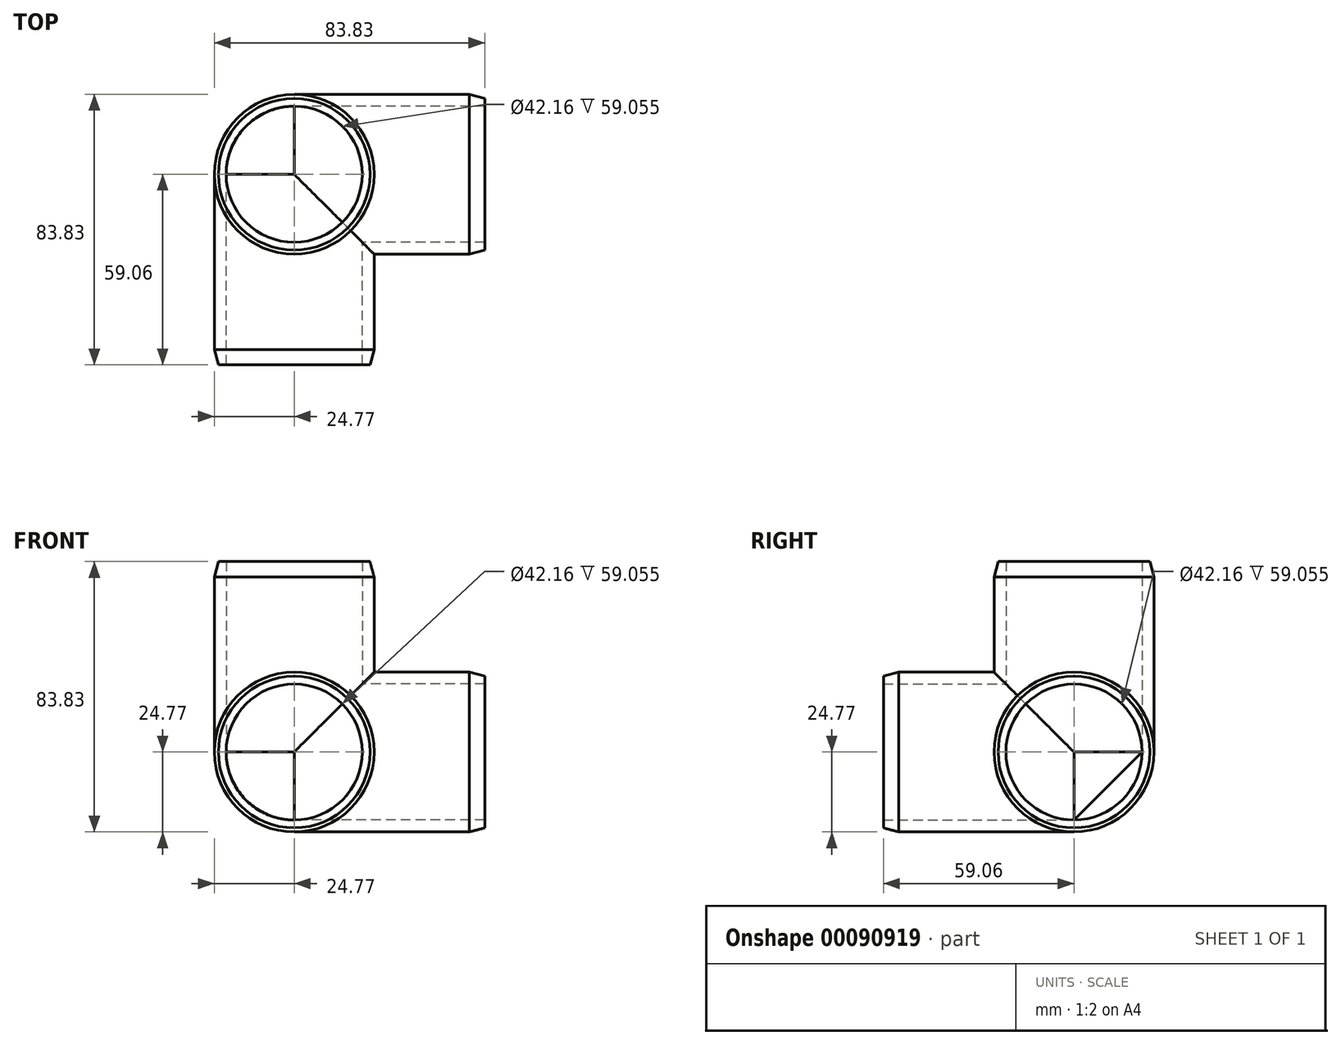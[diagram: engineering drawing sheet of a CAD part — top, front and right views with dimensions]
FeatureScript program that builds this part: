
annotation { "Feature Type Name" : "Feature", "Feature Type Description" : "" }
export const myFeature = defineFeature(function(context is Context, id is Id, definition is map)
    precondition{}
    {
        {
            var Q0;
            Q0=qCreatedBy(makeId("Front.planeOp"),FACE);
            var sketch = newSketch(context, id + "F0", { "sketchPlane" : qUnion([Q0])});
            skCircle(sketch, "E0", {"center": v(0, 0) * mm, "radius": 21.08 * mm});
            skCircle(sketch, "E1.0", {"center": v(0, 0) * mm, "radius": 24.77 * mm});
            skSolve(sketch);
        }
        {
            var Q0;
            Q0 = qSketchRegion(id + "F0", true);
            extrude(context, id + "F1", {"entities" : qUnion([Q0]), "depth" : 59.05 * mm});
        }
        {
            var Q0;
            Q0=qCreatedBy(makeId("Top.planeOp"),FACE);
            var sketch = newSketch(context, id + "F2", { "sketchPlane" : qUnion([Q0])});
            skCircle(sketch, "E2", {"center": v(0, 0) * mm, "radius": 21.08 * mm});
            skCircle(sketch, "E3.0", {"center": v(0, 0) * mm, "radius": 24.77 * mm});
            skSolve(sketch);
        }
        {
            var Q0;
            Q0 = qSketchRegion(id + "F2", true);
            extrude(context, id + "F3", {"entities" : qUnion([Q0]), "operationType" : NewBodyOperationType.ADD, "depth" : 59.05 * mm});
        }
        {
            var Q0;
            Q0=qCreatedBy(makeId("Right.planeOp"),FACE);
            var sketch = newSketch(context, id + "F4", { "sketchPlane" : qUnion([Q0])});
            skCircle(sketch, "E4", {"center": v(0, 0) * mm, "radius": 21.08 * mm});
            skCircle(sketch, "E5.0", {"center": v(0, 0) * mm, "radius": 24.77 * mm});
            skSolve(sketch);
        }
        {
            var Q0;
            Q0 = qSketchRegion(id + "F4", true);
            extrude(context, id + "F5", {"entities" : qUnion([Q0]), "operationType" : NewBodyOperationType.ADD, "depth" : 59.05 * mm});
        }
        {
            var Q0;
            Q0=makeQuery(id+"F4.imprint","IMPRINT",FACE,{"disambiguationData":[TD([[makeQuery(id+"F4.imprint","IMPRINT",EDGE,{"derivedFrom":sQuery(id+"F4.wireOp",EDGE,"E4")}),1.0]])]});
            extrude(context, id + "F6", {"entities" : qUnion([Q0]), "operationType" : NewBodyOperationType.REMOVE, "endBound" : BoundingType.THROUGH_ALL, "depth" : 25.4 * mm});
        }
        {
            var Q0;
            Q0=makeQuery(id+"F2.imprint","IMPRINT",FACE,{"disambiguationData":[TD([[makeQuery(id+"F2.imprint","IMPRINT",EDGE,{"derivedFrom":sQuery(id+"F2.wireOp",EDGE,"E2")}),1.0]])]});
            extrude(context, id + "F7", {"entities" : qUnion([Q0]), "operationType" : NewBodyOperationType.REMOVE, "endBound" : BoundingType.THROUGH_ALL, "depth" : 25.4 * mm});
        }
        {
            var Q0;
            Q0=makeQuery(id+"F0.imprint","IMPRINT",FACE,{"disambiguationData":[TD([[makeQuery(id+"F0.imprint","IMPRINT",EDGE,{"derivedFrom":sQuery(id+"F0.wireOp",EDGE,"E0")}),1.0]])]});
            extrude(context, id + "F8", {"entities" : qUnion([Q0]), "operationType" : NewBodyOperationType.REMOVE, "endBound" : BoundingType.THROUGH_ALL, "depth" : 25.4 * mm});
        }
        {
            var Q0;
            {var subQ0=sQuery(id+"F0.wireOp",EDGE,"E1.0");var subQ1=makeQuery(id+"F1.opExtrude","SWEPT_FACE",FACE,{"disambiguationData":[OSD([subQ0])]});var subQ2=sQuery(id+"F2.wireOp",EDGE,"E2");var subQ3=makeQuery(id+"F3.opExtrude","SWEPT_FACE",FACE,{"disambiguationData":[OSD([subQ2])]});var subQ4=sQuery(id+"F0.wireOp",EDGE,"E0");var subQ5=makeQuery(id+"F1.opExtrude","CAP_FACE",FACE,{"disambiguationData":[OSD([subQ4,subQ0])],"isStart":true});var subQ6=makeQuery(id+"F1.opExtrude","SWEPT_FACE",FACE,{"disambiguationData":[OSD([subQ4])]});var subQ7=sQuery(id+"F2.wireOp",EDGE,"E3.0");var subQ8=makeQuery(id+"F3.opExtrude","CAP_FACE",FACE,{"disambiguationData":[OSD([subQ2,subQ7])],"isStart":true});var subQ9=makeQuery(id+"F3.opExtrude","SWEPT_FACE",FACE,{"disambiguationData":[OSD([subQ7])]});var subQ10=sQuery(id+"F4.wireOp",EDGE,"E4");var subQ11=sQuery(id+"F4.wireOp",EDGE,"E5.0");Q0=makeQuery(id+"F5.boolean.opBoolean","SPLIT",FACE,{"disambiguationData":[TD([subQ6,subQ5,subQ1,subQ3,subQ8,subQ9,makeQuery(id+"F5.opExtrude","SWEPT_FACE",FACE,{"disambiguationData":[OSD([subQ10])]}),makeQuery(id+"F5.opExtrude","CAP_FACE",FACE,{"disambiguationData":[OSD([subQ10,subQ11])],"isStart":true}),makeQuery(id+"F5.opExtrude","SWEPT_FACE",FACE,{"disambiguationData":[OSD([subQ11])]})])],"derivedFrom":makeQuery(id+"F3.boolean.opBoolean","SPLIT",FACE,{"disambiguationData":[TD([subQ6,subQ5,subQ1,subQ3,subQ8,subQ9])],"derivedFrom":subQ5})});}
            var Q1;
            {var subQ0=sQuery(id+"F0.wireOp",EDGE,"E1.0");var subQ1=makeQuery(id+"F1.opExtrude","SWEPT_FACE",FACE,{"disambiguationData":[OSD([subQ0])]});var subQ2=sQuery(id+"F2.wireOp",EDGE,"E2");var subQ3=makeQuery(id+"F3.opExtrude","SWEPT_FACE",FACE,{"disambiguationData":[OSD([subQ2])]});var subQ4=sQuery(id+"F0.wireOp",EDGE,"E0");var subQ5=makeQuery(id+"F1.opExtrude","CAP_FACE",FACE,{"disambiguationData":[OSD([subQ4,subQ0])],"isStart":true});var subQ6=makeQuery(id+"F1.opExtrude","SWEPT_FACE",FACE,{"disambiguationData":[OSD([subQ4])]});var subQ7=sQuery(id+"F2.wireOp",EDGE,"E3.0");var subQ8=makeQuery(id+"F3.opExtrude","CAP_FACE",FACE,{"disambiguationData":[OSD([subQ2,subQ7])],"isStart":true});var subQ9=makeQuery(id+"F3.opExtrude","SWEPT_FACE",FACE,{"disambiguationData":[OSD([subQ7])]});var subQ10=sQuery(id+"F4.wireOp",EDGE,"E4");var subQ11=sQuery(id+"F4.wireOp",EDGE,"E5.0");Q1=makeQuery(id+"F5.boolean.opBoolean","SPLIT",FACE,{"disambiguationData":[TD([subQ6,subQ5,subQ1,subQ3,subQ8,subQ9,makeQuery(id+"F5.opExtrude","SWEPT_FACE",FACE,{"disambiguationData":[OSD([subQ10])]}),makeQuery(id+"F5.opExtrude","CAP_FACE",FACE,{"disambiguationData":[OSD([subQ10,subQ11])],"isStart":true}),makeQuery(id+"F5.opExtrude","SWEPT_FACE",FACE,{"disambiguationData":[OSD([subQ11])]})])],"derivedFrom":makeQuery(id+"F3.boolean.opBoolean","SPLIT",FACE,{"disambiguationData":[TD([subQ6,subQ5,subQ1,subQ3,subQ8,subQ9])],"derivedFrom":subQ8})});}
            var Q2;
            Q2=makeQuery(id+"F5.boolean.opBoolean","SPLIT",EDGE,{"disambiguationData":[OD(1.0)],"derivedFrom":makeQuery(id+"F5.opExtrude","CAP_EDGE",EDGE,{"disambiguationData":[OSD([sQuery(id+"F4.wireOp",EDGE,"E4")])],"isStart":true})});
            var Q3;
            {var subQ0=sQuery(id+"F0.wireOp",EDGE,"E1.0");var subQ1=sQuery(id+"F2.wireOp",EDGE,"E3.0");var subQ2=sQuery(id+"F4.wireOp",EDGE,"E5.0");Q3=makeQuery(id+"F5.boolean.opBoolean","SPLIT",EDGE,{"disambiguationData":[TD([makeQuery(id+"F1.opExtrude","CAP_FACE",FACE,{"disambiguationData":[OSD([sQuery(id+"F0.wireOp",EDGE,"E0"),subQ0])],"isStart":true}),makeQuery(id+"F1.opExtrude","SWEPT_FACE",FACE,{"disambiguationData":[OSD([subQ0])]}),makeQuery(id+"F3.opExtrude","CAP_FACE",FACE,{"disambiguationData":[OSD([sQuery(id+"F2.wireOp",EDGE,"E2"),subQ1])],"isStart":true}),makeQuery(id+"F3.opExtrude","SWEPT_FACE",FACE,{"disambiguationData":[OSD([subQ1])]}),makeQuery(id+"F5.opExtrude","CAP_FACE",FACE,{"disambiguationData":[OSD([sQuery(id+"F4.wireOp",EDGE,"E4"),subQ2])],"isStart":true}),makeQuery(id+"F5.opExtrude","SWEPT_FACE",FACE,{"disambiguationData":[OSD([subQ2])]})])],"derivedFrom":makeQuery(id+"F5.opExtrude","CAP_EDGE",EDGE,{"disambiguationData":[OSD([subQ2])],"isStart":true})});}
            loft(context, id + "F9", {"operationType" : NewBodyOperationType.ADD, "addGuides" : true, "sheetProfilesArray" : [{ "sheetProfileEntities" : qUnion([Q0]) }, { "sheetProfileEntities" : qUnion([Q1]) }], "guidesArray" : [{ "guideEntities" : qUnion([Q2]), "guideDerivativeType" : LoftGuideDerivativeType.DEFAULT, "guideDerivativeMagnitude" : 1 }, { "guideEntities" : qUnion([Q3]), "guideDerivativeType" : LoftGuideDerivativeType.DEFAULT, "guideDerivativeMagnitude" : 1 }]});
        }
        {
            var Q0;
            Q0=makeQuery(id+"F3.opExtrude","CAP_EDGE",EDGE,{"disambiguationData":[OSD([sQuery(id+"F2.wireOp",EDGE,"E3.0")])],"isStart":false});
            var Q1;
            Q1=makeQuery(id+"F1.opExtrude","CAP_EDGE",EDGE,{"disambiguationData":[OSD([sQuery(id+"F0.wireOp",EDGE,"E1.0")])],"isStart":false});
            var Q2;
            Q2=makeQuery(id+"F5.opExtrude","CAP_EDGE",EDGE,{"disambiguationData":[OSD([sQuery(id+"F4.wireOp",EDGE,"E5.0")])],"isStart":false});
            chamfer(context, id + "F10", {"entities" : qUnion([Q0, Q1, Q2]), "chamferType" : ChamferType.OFFSET_ANGLE, "width" : 1.27 * mm, "oppositeDirection" : false, "angle" : 75 * degree, "tangentPropagation" : true});
        }
    });
